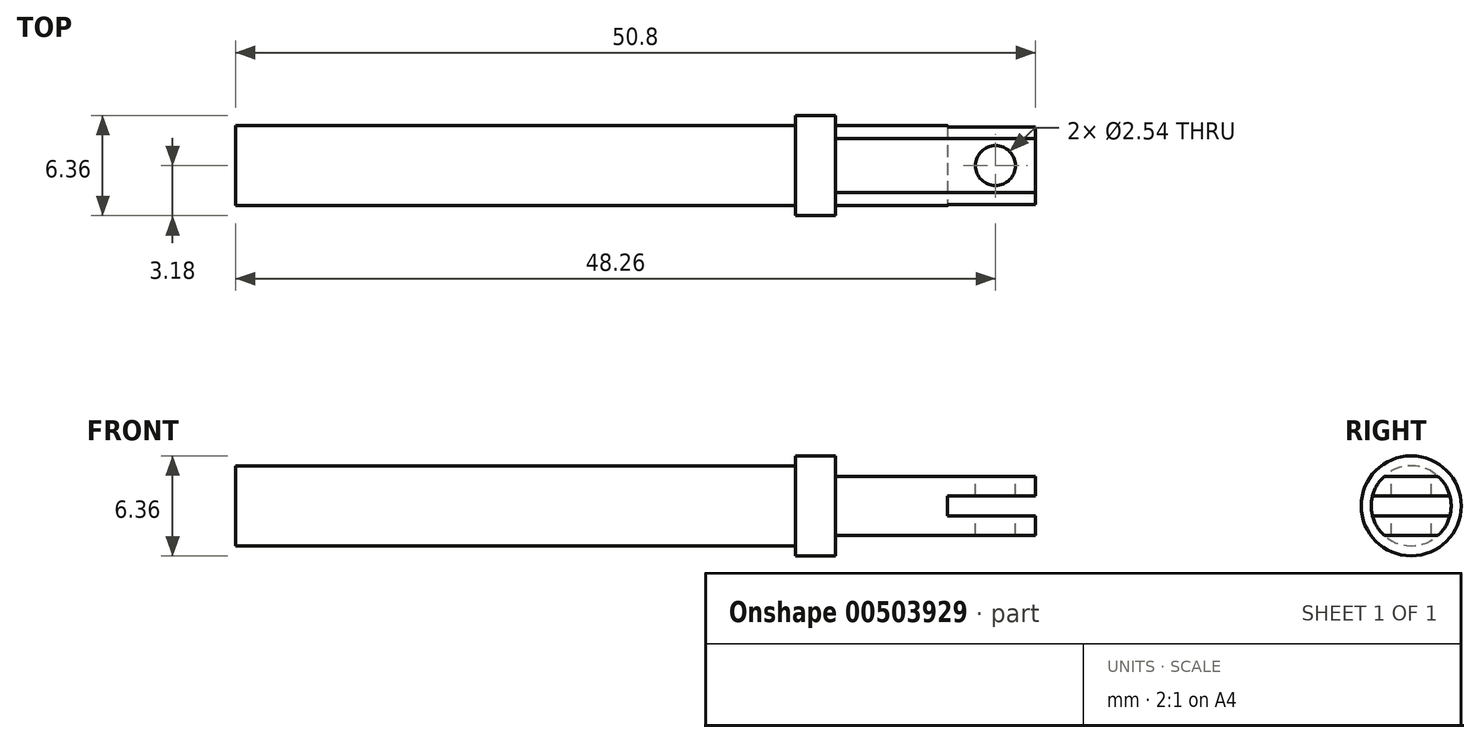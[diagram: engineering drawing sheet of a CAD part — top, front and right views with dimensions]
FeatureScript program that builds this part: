
annotation { "Feature Type Name" : "Feature", "Feature Type Description" : "" }
export const myFeature = defineFeature(function(context is Context, id is Id, definition is map)
    precondition{}
    {
        {
            var Q0;
            Q0=qCreatedBy(makeId("Right.planeOp"),FACE);
            var sketch = newSketch(context, id + "F0", { "sketchPlane" : qUnion([Q0])});
            skCircle(sketch, "E0", {"center": v(0, 0) * mm, "radius": 2.54 * mm});
            skSolve(sketch);
        }
        {
            var Q0;
            Q0=makeQuery(id+"F0.imprint","IMPRINT",FACE,{"disambiguationData":[TD([[makeQuery(id+"F0.imprint","IMPRINT",EDGE,{"derivedFrom":sQuery(id+"F0.wireOp",EDGE,"E0")}),1.0]])]});
            extrude(context, id + "F1", {"entities" : qUnion([Q0]), "depth" : 50.8 * mm});
        }
        {
            var Q0;
            Q0=makeQuery(id+"F1.opExtrude","CAP_FACE",FACE,{"disambiguationData":[OSD([sQuery(id+"F0.wireOp",EDGE,"E0")])],"isStart":false});
            var sketch = newSketch(context, id + "F2", { "sketchPlane" : qUnion([Q0])});
            skLineSegment(sketch, "E1.bottom", {"start": v(1.7, -1.88) * mm, "end": v(-1.7, -1.88) * mm});
            skLineSegment(sketch, "E1.top", {"start": v(1.7, -3.2) * mm, "end": v(-1.7, -3.2) * mm});
            skLineSegment(sketch, "E1.left", {"start": v(1.7, -1.88) * mm, "end": v(1.7, -3.2) * mm});
            skLineSegment(sketch, "E1.right", {"start": v(-1.7, -1.88) * mm, "end": v(-1.7, -3.2) * mm});
            skPoint(sketch, "E1.middle", {"position": v(0, -2.54) * mm});
            skLineSegment(sketch, "E2", {"start": v(1.7, -1.88) * mm, "end": v(1.7, 1.88) * mm});
            skLineSegment(sketch, "E3", {"start": v(-1.7, -1.88) * mm, "end": v(-1.7, 1.88) * mm});
            skLineSegment(sketch, "E4.bottom", {"start": v(1.7, 1.88) * mm, "end": v(-1.7, 1.88) * mm});
            skLineSegment(sketch, "E4.top", {"start": v(1.7, 3.2) * mm, "end": v(-1.7, 3.2) * mm});
            skLineSegment(sketch, "E4.left", {"start": v(1.7, 1.88) * mm, "end": v(1.7, 3.2) * mm});
            skLineSegment(sketch, "E4.right", {"start": v(-1.7, 1.88) * mm, "end": v(-1.7, 3.2) * mm});
            skPoint(sketch, "E4.middle", {"position": v(0, 2.54) * mm});
            skSolve(sketch);
        }
        {
            var Q0;
            Q0=makeQuery(id+"F2.imprint","IMPRINT",FACE,{"disambiguationData":[TD([[makeQuery(id+"F2.imprint","IMPRINT",EDGE,{"derivedFrom":sQuery(id+"F2.wireOp",EDGE,"E1.top")}),-1.0]])]});
            var Q1;
            {var subQ0=sQuery(id+"F2.wireOp",EDGE,"E1.bottom");Q1=makeQuery(id+"F2.imprint","IMPRINT",FACE,{"disambiguationData":[TD([[makeQuery(id+"F2.imprint","IMPRINT",EDGE,{"derivedFrom":subQ0}),1.0]])]});}
            var Q2;
            {var subQ0=sQuery(id+"F2.wireOp",EDGE,"E4.bottom");Q2=makeQuery(id+"F2.imprint","IMPRINT",FACE,{"disambiguationData":[TD([[makeQuery(id+"F2.imprint","IMPRINT",EDGE,{"derivedFrom":subQ0}),-1.0]])]});}
            var Q3;
            Q3=makeQuery(id+"F2.imprint","IMPRINT",FACE,{"disambiguationData":[TD([[makeQuery(id+"F2.imprint","IMPRINT",EDGE,{"derivedFrom":sQuery(id+"F2.wireOp",EDGE,"E4.top")}),1.0]])]});
            extrude(context, id + "F3", {"entities" : qUnion([Q0, Q1, Q2, Q3]), "operationType" : NewBodyOperationType.REMOVE, "oppositeDirection" : true, "depth" : 12.7 * mm});
        }
        {
            var Q0;
            Q0=makeQuery(id+"F1.opExtrude","CAP_FACE",FACE,{"disambiguationData":[OSD([sQuery(id+"F0.wireOp",EDGE,"E0")])],"isStart":false});
            var sketch = newSketch(context, id + "F4", { "sketchPlane" : qUnion([Q0])});
            skLineSegment(sketch, "E5.bottom", {"start": v(2.7, 0.64) * mm, "end": v(-2.7, 0.64) * mm});
            skLineSegment(sketch, "E5.top", {"start": v(2.7, -0.64) * mm, "end": v(-2.7, -0.64) * mm});
            skLineSegment(sketch, "E5.left", {"start": v(2.7, 0.64) * mm, "end": v(2.7, -0.64) * mm});
            skLineSegment(sketch, "E5.right", {"start": v(-2.7, 0.64) * mm, "end": v(-2.7, -0.64) * mm});
            skPoint(sketch, "E5.middle", {"position": v(0, 0) * mm});
            skSolve(sketch);
        }
        {
            var Q0;
            Q0 = qSketchRegion(id + "F4", true);
            extrude(context, id + "F5", {"entities" : qUnion([Q0]), "operationType" : NewBodyOperationType.REMOVE, "oppositeDirection" : true, "depth" : 5.6 * mm});
        }
        {
            var Q0;
            Q0=makeQuery(id+"F3.boolean.opBoolean","COPY",FACE,{"derivedFrom":makeQuery(id+"F3.opExtrude","SWEPT_FACE",FACE,{"disambiguationData":[OSD([sQuery(id+"F2.wireOp",EDGE,"E4.bottom")])]})});
            var sketch = newSketch(context, id + "F6", { "sketchPlane" : qUnion([Q0])});
            skCircle(sketch, "E6", {"center": v(48.26, 0) * mm, "radius": 1.27 * mm});
            skLineSegment(sketch, "E7", {"start": v(48.26, 0) * mm, "end": v(50.8, 0) * mm});
            skSolve(sketch);
        }
        {
            var Q0;
            Q0=makeQuery(id+"F6.imprint","IMPRINT",FACE,{"disambiguationData":[TD([[makeQuery(id+"F6.imprint","IMPRINT",EDGE,{"derivedFrom":sQuery(id+"F6.wireOp",EDGE,"E6")}),1.0]])]});
            extrude(context, id + "F7", {"entities" : qUnion([Q0]), "operationType" : NewBodyOperationType.REMOVE, "oppositeDirection" : true, "depth" : 25.4 * mm});
        }
        {
            var Q0;
            {var subQ0=sQuery(id+"F0.wireOp",EDGE,"E0");Q0=makeQuery(id+"F5.boolean.opBoolean","SPLIT",FACE,{"disambiguationData":[TD([makeQuery(id+"F3.boolean.opBoolean","COPY",FACE,{"derivedFrom":makeQuery(id+"F3.opExtrude","SWEPT_FACE",FACE,{"disambiguationData":[OSD([sQuery(id+"F2.wireOp",EDGE,"E4.bottom")])]})})])],"derivedFrom":makeQuery(id+"F1.opExtrude","CAP_FACE",FACE,{"disambiguationData":[OSD([subQ0])],"isStart":false})});}
            var sketch = newSketch(context, id + "F8", { "sketchPlane" : qUnion([Q0])});
            skCircle(sketch, "E8", {"center": v(0, 0) * mm, "radius": 3.18 * mm});
            skSolve(sketch);
        }
        {
            var Q0;
            Q0=makeQuery(id+"F8.imprint","IMPRINT",FACE,{"disambiguationData":[TD([[makeQuery(id+"F8.imprint","IMPRINT",EDGE,{"derivedFrom":sQuery(id+"F8.wireOp",EDGE,"E8")}),1.0]])]});
            extrude(context, id + "F9", {"entities" : qUnion([Q0]), "operationType" : NewBodyOperationType.ADD, "oppositeDirection" : true, "depth" : 15.24 * mm, "hasSecondDirection" : true, "secondDirectionOppositeDirection" : true, "secondDirectionDepth" : 12.7 * mm});
        }
    });
